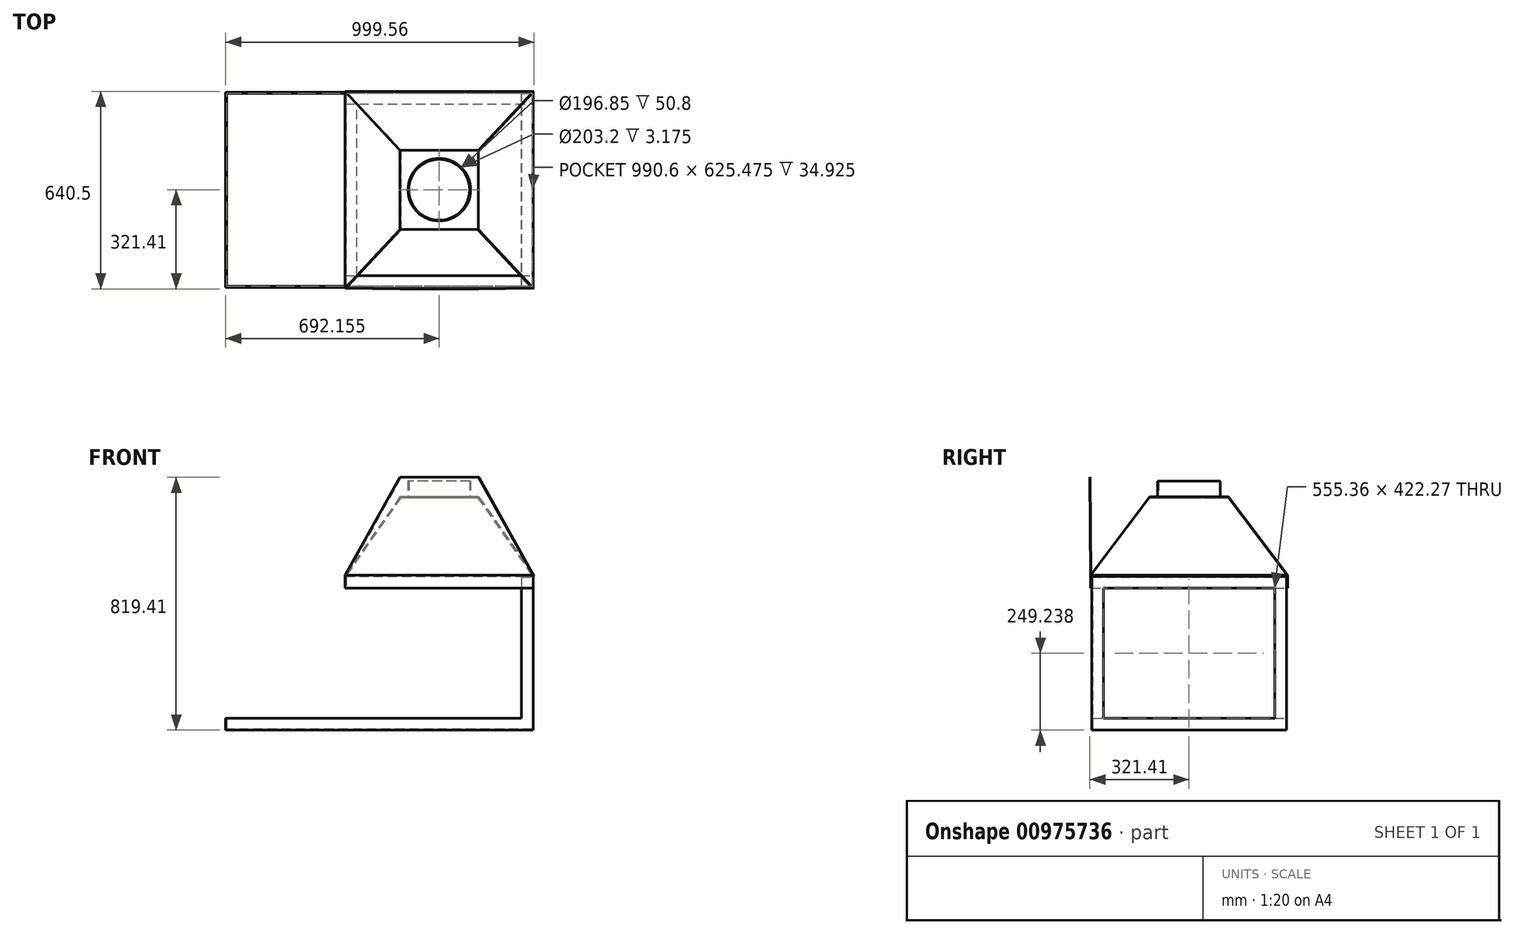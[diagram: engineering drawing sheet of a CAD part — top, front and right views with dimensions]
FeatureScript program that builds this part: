
annotation { "Feature Type Name" : "Feature", "Feature Type Description" : "" }
export const myFeature = defineFeature(function(context is Context, id is Id, definition is map)
    precondition{}
    {
        {
            var Q0;
            Q0=qCreatedBy(makeId("Top.planeOp"),FACE);
            var sketch = newSketch(context, id + "F0", { "sketchPlane" : qUnion([Q0])});
            skLineSegment(sketch, "E0.bottom", {"start": v(498.48, -315.91) * mm, "end": v(-498.48, -315.91) * mm});
            skLineSegment(sketch, "E0.top", {"start": v(498.48, 315.91) * mm, "end": v(-498.48, 315.91) * mm});
            skLineSegment(sketch, "E0.left", {"start": v(498.48, -315.91) * mm, "end": v(498.48, 315.91) * mm});
            skLineSegment(sketch, "E0.right", {"start": v(-498.48, -315.91) * mm, "end": v(-498.48, 315.91) * mm});
            skPoint(sketch, "E0.middle", {"position": v(0, 0) * mm});
            skLineSegment(sketch, "E1.0", {"start": v(495.3, 312.74) * mm, "end": v(-495.3, 312.74) * mm});
            skLineSegment(sketch, "E1.1", {"start": v(495.3, -312.74) * mm, "end": v(495.3, 312.74) * mm});
            skLineSegment(sketch, "E1.2", {"start": v(495.3, -312.74) * mm, "end": v(-495.3, -312.74) * mm});
            skLineSegment(sketch, "E1.3", {"start": v(-495.3, -312.74) * mm, "end": v(-495.3, 312.74) * mm});
            skSolve(sketch);
        }
        {
            var Q0;
            Q0=makeQuery(id+"F0.imprint","IMPRINT",FACE,{"disambiguationData":[TD([[makeQuery(id+"F0.imprint","IMPRINT",EDGE,{"derivedFrom":sQuery(id+"F0.wireOp",EDGE,"E0.bottom")}),-1.0]])]});
            extrude(context, id + "F1", {"entities" : qUnion([Q0]), "depth" : 38.1 * mm, "offsetDistance" : 25.4 * mm});
        }
        {
            var Q0;
            Q0=makeQuery(id+"F1.opExtrude","CAP_FACE",FACE,{"disambiguationData":[OSD([sQuery(id+"F0.wireOp",EDGE,"E0.bottom"),sQuery(id+"F0.wireOp",EDGE,"E0.top"),sQuery(id+"F0.wireOp",EDGE,"E0.left"),sQuery(id+"F0.wireOp",EDGE,"E0.right"),sQuery(id+"F0.wireOp",EDGE,"E1.0"),sQuery(id+"F0.wireOp",EDGE,"E1.1"),sQuery(id+"F0.wireOp",EDGE,"E1.2"),sQuery(id+"F0.wireOp",EDGE,"E1.3")])],"isStart":false});
            var sketch = newSketch(context, id + "F2", { "sketchPlane" : qUnion([Q0])});
            skLineSegment(sketch, "E2", {"start": v(496.98, 315.91) * mm, "end": v(496.98, 277.81) * mm, "construction": true});
            skLineSegment(sketch, "E3", {"start": v(498.48, 314.56) * mm, "end": v(460.38, 314.56) * mm, "construction": true});
            skLineSegment(sketch, "E4", {"start": v(460.38, 315.91) * mm, "end": v(460.38, 312.74) * mm});
            skLineSegment(sketch, "E5", {"start": v(460.38, 312.74) * mm, "end": v(495.3, 312.74) * mm});
            skLineSegment(sketch, "E6", {"start": v(495.3, 312.74) * mm, "end": v(495.3, 277.81) * mm});
            skLineSegment(sketch, "E7", {"start": v(495.3, 277.68) * mm, "end": v(498.48, 277.68) * mm});
            skLineSegment(sketch, "E8", {"start": v(498.48, 277.68) * mm, "end": v(498.48, 315.91) * mm});
            skLineSegment(sketch, "E9", {"start": v(498.48, 315.91) * mm, "end": v(460.38, 315.91) * mm});
            skSolve(sketch);
        }
        {
            var Q0;
            Q0=makeQuery(id+"F2.imprint","IMPRINT",FACE,{"disambiguationData":[TD([[makeQuery(id+"F2.imprint","IMPRINT",EDGE,{"derivedFrom":sQuery(id+"F2.wireOp",EDGE,"E4")}),1.0]])]});
            extrude(context, id + "F3", {"entities" : qUnion([Q0]), "depth" : 460.38 * mm, "offsetDistance" : 25.4 * mm});
        }
        {
            var Q0;
            Q0=makeQuery(id+"F3.opExtrude","SWEPT_BODY",BODY,{"disambiguationData":[OSD([sQuery(id+"F0.wireOp",EDGE,"E1.1"),sQuery(id+"F2.wireOp",EDGE,"E4"),sQuery(id+"F2.wireOp",EDGE,"E5"),sQuery(id+"F2.wireOp",EDGE,"E6"),sQuery(id+"F2.wireOp",EDGE,"E7"),sQuery(id+"F2.wireOp",EDGE,"E8"),sQuery(id+"F2.wireOp",EDGE,"E9")])]});
            var Q1;
            Q1=qCreatedBy(makeId("Front.planeOp"),FACE);
            mirror(context, id + "F4", {"operationType" : NewBodyOperationType.ADD, "entities" : qUnion([Q0]), "mirrorPlane" : qUnion([Q1])});
        }
        {
            var Q0;
            Q0=makeQuery(id+"F3.opExtrude","SWEPT_FACE",FACE,{"disambiguationData":[OSD([sQuery(id+"F2.wireOp",EDGE,"E7")])]});
            var sketch = newSketch(context, id + "F5", { "sketchPlane" : qUnion([Q0])});
            skLineSegment(sketch, "E10", {"start": v(496.89, 498.48) * mm, "end": v(496.89, 460.38) * mm, "construction": true});
            skLineSegment(sketch, "E11", {"start": v(495.3, 460.38) * mm, "end": v(498.48, 460.38) * mm});
            skLineSegment(sketch, "E12", {"start": v(495.3, 460.38) * mm, "end": v(495.3, 498.48) * mm});
            skLineSegment(sketch, "E13", {"start": v(495.3, 498.48) * mm, "end": v(498.48, 498.48) * mm});
            skLineSegment(sketch, "E14", {"start": v(498.48, 498.48) * mm, "end": v(498.48, 460.38) * mm});
            skSolve(sketch);
        }
        {
            var Q0;
            Q0=makeQuery(id+"F4.boolean.opBoolean","MERGE",FACE,{"derivedFrom":[makeQuery(id+"F1.opExtrude","SWEPT_FACE",FACE,{"disambiguationData":[OSD([sQuery(id+"F0.wireOp",EDGE,"E1.0")])]}),makeQuery(id+"F3.opExtrude","SWEPT_FACE",FACE,{"disambiguationData":[OSD([sQuery(id+"F2.wireOp",EDGE,"E5")])]})]});
            var sketch = newSketch(context, id + "F6", { "sketchPlane" : qUnion([Q0])});
            skPoint(sketch, "E15.0", {"position": v(477.84, 498.48) * mm});
            skLineSegment(sketch, "E16", {"start": v(477.84, 498.48) * mm, "end": v(477.84, 495.3) * mm, "construction": true});
            skLineSegment(sketch, "E17", {"start": v(460.38, 495.3) * mm, "end": v(495.3, 495.3) * mm});
            skLineSegment(sketch, "E18", {"start": v(495.3, 495.3) * mm, "end": v(495.3, 498.48) * mm});
            skLineSegment(sketch, "E19", {"start": v(495.3, 498.48) * mm, "end": v(460.38, 498.48) * mm});
            skLineSegment(sketch, "E20", {"start": v(460.38, 498.48) * mm, "end": v(460.38, 495.3) * mm});
            skSolve(sketch);
        }
        {
            var Q0;
            Q0=makeQuery(id+"F6.imprint","IMPRINT",FACE,{"disambiguationData":[TD([[makeQuery(id+"F6.imprint","IMPRINT",EDGE,{"derivedFrom":sQuery(id+"F6.wireOp",EDGE,"E17")}),1.0]])]});
            var Q1;
            Q1=makeQuery(id+"F4.boolean.opBoolean","MERGE",FACE,{"derivedFrom":[makeQuery(id+"F1.opExtrude","SWEPT_FACE",FACE,{"disambiguationData":[OSD([sQuery(id+"F0.wireOp",EDGE,"E1.2")])]}),makeQuery(id+"F4.opPattern","COPY",FACE,{"derivedFrom":makeQuery(id+"F3.opExtrude","SWEPT_FACE",FACE,{"disambiguationData":[OSD([sQuery(id+"F2.wireOp",EDGE,"E5")])]}),"instanceName":"1"})]});
            extrude(context, id + "F7", {"entities" : qUnion([Q0]), "operationType" : NewBodyOperationType.ADD, "endBound" : BoundingType.UP_TO_SURFACE, "depth" : 25.4 * mm, "endBoundEntityFace" : qUnion([Q1]), "offsetDistance" : 25.4 * mm});
        }
        {
            var Q0;
            Q0=makeQuery(id+"F5.imprint","IMPRINT",FACE,{"disambiguationData":[TD([[makeQuery(id+"F5.imprint","IMPRINT",EDGE,{"derivedFrom":sQuery(id+"F5.wireOp",EDGE,"E11")}),1.0]])]});
            var Q1;
            Q1=makeQuery(id+"F4.opPattern","COPY",FACE,{"derivedFrom":makeQuery(id+"F3.opExtrude","SWEPT_FACE",FACE,{"disambiguationData":[OSD([sQuery(id+"F2.wireOp",EDGE,"E7")])]}),"instanceName":"1"});
            extrude(context, id + "F8", {"entities" : qUnion([Q0]), "operationType" : NewBodyOperationType.ADD, "endBound" : BoundingType.UP_TO_SURFACE, "depth" : 25.4 * mm, "endBoundEntityFace" : qUnion([Q1]), "offsetDistance" : 25.4 * mm});
        }
        {
            var Q0;
            {var subQ0=makeQuery(id+"F3.opExtrude","SWEPT_FACE",FACE,{"disambiguationData":[OSD([sQuery(id+"F2.wireOp",EDGE,"E8")])]});Q0=makeQuery(id+"F8.boolean.opBoolean","MERGE",FACE,{"derivedFrom":[makeQuery(id+"F4.boolean.opBoolean","MERGE",FACE,{"derivedFrom":[makeQuery(id+"F1.opExtrude","SWEPT_FACE",FACE,{"disambiguationData":[OSD([sQuery(id+"F0.wireOp",EDGE,"E0.left")])]}),subQ0,makeQuery(id+"F4.opPattern","COPY",FACE,{"derivedFrom":subQ0,"instanceName":"1"})]}),makeQuery(id+"F8.opExtrude","SWEPT_FACE",FACE,{"disambiguationData":[OSD([sQuery(id+"F5.wireOp",EDGE,"E14")])]})]});}
            var sketch = newSketch(context, id + "F9", { "sketchPlane" : qUnion([Q0])});
            skPoint(sketch, "E21.0", {"position": v(315.91, 498.48) * mm});
            skLineSegment(sketch, "E22", {"start": v(315.91, 498.48) * mm, "end": v(277.81, 498.48) * mm});
            skLineSegment(sketch, "E23", {"start": v(315.91, 498.48) * mm, "end": v(315.91, 460.38) * mm});
            skLineSegment(sketch, "E24", {"start": v(315.91, 460.38) * mm, "end": v(319.09, 460.38) * mm});
            skLineSegment(sketch, "E25", {"start": v(277.81, 498.48) * mm, "end": v(277.81, 501.65) * mm});
            skLineSegment(sketch, "E26", {"start": v(277.81, 501.65) * mm, "end": v(319.09, 501.65) * mm});
            skLineSegment(sketch, "E27", {"start": v(319.09, 501.65) * mm, "end": v(319.09, 460.38) * mm});
            skSolve(sketch);
        }
        {
            var Q0;
            Q0=makeQuery(id+"F9.imprint","IMPRINT",FACE,{"disambiguationData":[TD([[makeQuery(id+"F9.imprint","IMPRINT",EDGE,{"derivedFrom":sQuery(id+"F9.wireOp",EDGE,"E22")}),1.0]])]});
            extrude(context, id + "F10", {"entities" : qUnion([Q0]), "oppositeDirection" : true, "depth" : 609.6 * mm, "offsetDistance" : 25.4 * mm});
        }
        {
            var Q0;
            Q0=makeQuery(id+"F10.opExtrude","SWEPT_BODY",BODY,{"disambiguationData":[OSD([sQuery(id+"F9.wireOp",EDGE,"E22"),sQuery(id+"F9.wireOp",EDGE,"E23"),sQuery(id+"F9.wireOp",EDGE,"E24"),sQuery(id+"F9.wireOp",EDGE,"E25"),sQuery(id+"F9.wireOp",EDGE,"E26"),sQuery(id+"F9.wireOp",EDGE,"E27")])]});
            var Q1;
            Q1=qCreatedBy(makeId("Front.planeOp"),FACE);
            mirror(context, id + "F11", {"entities" : qUnion([Q0]), "mirrorPlane" : qUnion([Q1])});
        }
        {
            var Q0;
            Q0=makeQuery(id+"F10.opExtrude","SWEPT_FACE",FACE,{"disambiguationData":[OSD([sQuery(id+"F9.wireOp",EDGE,"E23")])]});
            var sketch = newSketch(context, id + "F12", { "sketchPlane" : qUnion([Q0])});
            skPoint(sketch, "E28.0", {"position": v(-111.13, 460.38) * mm});
            skLineSegment(sketch, "E29", {"start": v(-111.13, 460.37) * mm, "end": v(-107.95, 460.37) * mm});
            skLineSegment(sketch, "E30", {"start": v(-107.95, 460.37) * mm, "end": v(-107.95, 498.48) * mm});
            skLineSegment(sketch, "E31", {"start": v(-107.95, 498.48) * mm, "end": v(-111.12, 498.48) * mm});
            skLineSegment(sketch, "E32", {"start": v(-111.12, 498.48) * mm, "end": v(-111.13, 460.38) * mm});
            skSolve(sketch);
        }
        {
            var Q0;
            Q0=makeQuery(id+"F12.imprint","IMPRINT",FACE,{"disambiguationData":[TD([[makeQuery(id+"F12.imprint","IMPRINT",EDGE,{"derivedFrom":sQuery(id+"F12.wireOp",EDGE,"E29")}),1.0]])]});
            var Q1;
            Q1=makeQuery(id+"F11.opPattern","COPY",FACE,{"derivedFrom":makeQuery(id+"F10.opExtrude","SWEPT_FACE",FACE,{"disambiguationData":[OSD([sQuery(id+"F9.wireOp",EDGE,"E23")])]}),"instanceName":"1"});
            extrude(context, id + "F13", {"entities" : qUnion([Q0]), "endBound" : BoundingType.UP_TO_SURFACE, "depth" : 25.4 * mm, "endBoundEntityFace" : qUnion([Q1]), "offsetDistance" : 25.4 * mm});
        }
        {
            var Q0;
            Q0=makeQuery(id+"F10.opExtrude","SWEPT_FACE",FACE,{"disambiguationData":[OSD([sQuery(id+"F9.wireOp",EDGE,"E25")])]});
            var sketch = newSketch(context, id + "F14", { "sketchPlane" : qUnion([Q0])});
            skLineSegment(sketch, "E33", {"start": v(-111.13, 500.06) * mm, "end": v(-73.03, 500.06) * mm, "construction": true});
            skLineSegment(sketch, "E34", {"start": v(-73.03, 501.65) * mm, "end": v(-73.03, 498.48) * mm});
            skLineSegment(sketch, "E35", {"start": v(-73.03, 498.48) * mm, "end": v(-111.12, 498.48) * mm});
            skLineSegment(sketch, "E36", {"start": v(-111.13, 498.48) * mm, "end": v(-111.13, 501.65) * mm});
            skLineSegment(sketch, "E37", {"start": v(-111.13, 501.65) * mm, "end": v(-73.03, 501.65) * mm});
            skSolve(sketch);
        }
        {
            var Q0;
            Q0=makeQuery(id+"F14.imprint","IMPRINT",FACE,{"disambiguationData":[TD([[makeQuery(id+"F14.imprint","IMPRINT",EDGE,{"derivedFrom":sQuery(id+"F14.wireOp",EDGE,"E34")}),-1.0]])]});
            var Q1;
            Q1=makeQuery(id+"F11.opPattern","COPY",FACE,{"derivedFrom":makeQuery(id+"F10.opExtrude","SWEPT_FACE",FACE,{"disambiguationData":[OSD([sQuery(id+"F9.wireOp",EDGE,"E25")])]}),"instanceName":"1"});
            extrude(context, id + "F15", {"entities" : qUnion([Q0]), "endBound" : BoundingType.UP_TO_SURFACE, "depth" : 25.4 * mm, "endBoundEntityFace" : qUnion([Q1]), "offsetDistance" : 25.4 * mm});
        }
        {
            var Q0;
            Q0=makeQuery(id+"F11.opPattern","COPY",FACE,{"derivedFrom":makeQuery(id+"F10.opExtrude","SWEPT_FACE",FACE,{"disambiguationData":[OSD([sQuery(id+"F9.wireOp",EDGE,"E26")])]}),"instanceName":"1"});
            var sketch = newSketch(context, id + "F16", { "sketchPlane" : qUnion([Q0])});
            skPoint(sketch, "E38.0", {"position": v(498.48, -319.09) * mm});
            skPoint(sketch, "E39.0", {"position": v(-111.13, 319.09) * mm});
            skPoint(sketch, "E40.0", {"position": v(498.48, 319.09) * mm});
            skPoint(sketch, "E41.0", {"position": v(-111.13, -319.09) * mm});
            skPoint(sketch, "E42.0", {"position": v(193.67, 319.09) * mm});
            skLineSegment(sketch, "E43", {"start": v(193.67, 319.09) * mm, "end": v(193.67, -319.09) * mm, "construction": true});
            skCircle(sketch, "E44", {"center": v(193.67, 0) * mm, "radius": 76.2 * mm});
            skSolve(sketch);
        }
        {
            var Q0;
            Q0=qCreatedBy(makeId("Front.planeOp"),FACE);
            var sketch = newSketch(context, id + "F17", { "sketchPlane" : qUnion([Q0])});
            skPoint(sketch, "E45.0", {"position": v(193.67, 501.65) * mm});
            skLineSegment(sketch, "E46", {"start": v(193.67, 501.65) * mm, "end": v(193.67, 755.65) * mm, "construction": true});
            skSolve(sketch);
        }
        {
            var Q0;
            Q0=makeQuery(id+"F10.opExtrude","SWEPT_FACE",FACE,{"disambiguationData":[OSD([sQuery(id+"F9.wireOp",EDGE,"E26")])]});
            cPlane(context, id + "F18", {"entities" : qUnion([Q0]), "cplaneType" : CPlaneType.OFFSET, "offset" : 254 * mm, "width" : 152.4 * mm, "height" : 152.4 * mm});
        }
        {
            var Q0;
            Q0=qCreatedBy(id+"F18.planeOp",FACE);
            var sketch = newSketch(context, id + "F19", { "sketchPlane" : qUnion([Q0])});
            skPoint(sketch, "E47.0", {"position": v(193.67, 0) * mm});
            skCircle(sketch, "E48", {"center": v(193.67, 0) * mm, "radius": 101.6 * mm});
            skLineSegment(sketch, "E49.bottom", {"start": v(320.67, -128.15) * mm, "end": v(66.67, -128.15) * mm});
            skLineSegment(sketch, "E49.top", {"start": v(320.67, 128.15) * mm, "end": v(66.67, 128.15) * mm});
            skLineSegment(sketch, "E49.left", {"start": v(320.67, -128.15) * mm, "end": v(320.67, 128.15) * mm});
            skLineSegment(sketch, "E49.right", {"start": v(66.67, -128.15) * mm, "end": v(66.67, 128.15) * mm});
            skSolve(sketch);
        }
        {
            var Q0;
            Q0=sQuery(id+"F19.wireOp",VERTEX,"E49.bottom.end");
            var Q1;
            Q1=sQuery(id+"F16.wireOp",VERTEX,"E41.0");
            var Q2;
            Q2=sQuery(id+"F16.wireOp",VERTEX,"E38.0");
            cPlane(context, id + "F20", {"entities" : qUnion([Q0, Q1, Q2]), "cplaneType" : CPlaneType.THREE_POINT, "offset" : 25.4 * mm, "width" : 152.4 * mm, "height" : 152.4 * mm});
        }
        {
            var Q0;
            Q0=qCreatedBy(id+"F20.planeOp",FACE);
            var sketch = newSketch(context, id + "F21", { "sketchPlane" : qUnion([Q0])});
            skPoint(sketch, "E50.0", {"position": v(-66.67, 527.02) * mm});
            skPoint(sketch, "E51.0", {"position": v(111.13, 209.25) * mm});
            skPoint(sketch, "E52.0", {"position": v(-320.67, 527.02) * mm});
            skPoint(sketch, "E53.0", {"position": v(-498.48, 209.25) * mm});
            skLineSegment(sketch, "E54", {"start": v(-66.67, 527.02) * mm, "end": v(111.13, 209.25) * mm});
            skLineSegment(sketch, "E55", {"start": v(-320.67, 527.02) * mm, "end": v(-498.47, 209.25) * mm});
            skLineSegment(sketch, "E56", {"start": v(-498.47, 209.25) * mm, "end": v(111.13, 209.25) * mm});
            skLineSegment(sketch, "E57", {"start": v(-66.67, 527.02) * mm, "end": v(-320.67, 527.02) * mm});
            skSolve(sketch);
        }
        {
            var Q0;
            Q0=sQuery(id+"F19.wireOp",VERTEX,"E49.top.end");
            var Q1;
            Q1=sQuery(id+"F16.wireOp",VERTEX,"E39.0");
            var Q2;
            Q2=sQuery(id+"F16.wireOp",VERTEX,"E41.0");
            cPlane(context, id + "F22", {"entities" : qUnion([Q0, Q1, Q2]), "cplaneType" : CPlaneType.THREE_POINT, "offset" : 25.4 * mm, "width" : 152.4 * mm, "height" : 152.4 * mm});
        }
        {
            var Q0;
            Q0=qCreatedBy(id+"F22.planeOp",FACE);
            var sketch = newSketch(context, id + "F23", { "sketchPlane" : qUnion([Q0])});
            skPoint(sketch, "E58.0", {"position": v(128.15, 657.29) * mm});
            skPoint(sketch, "E59.0", {"position": v(-128.15, 657.29) * mm});
            skPoint(sketch, "E60.0", {"position": v(319.09, 347.24) * mm});
            skPoint(sketch, "E61.0", {"position": v(-319.09, 347.24) * mm});
            skLineSegment(sketch, "E62", {"start": v(128.15, 657.29) * mm, "end": v(319.09, 347.24) * mm});
            skLineSegment(sketch, "E63", {"start": v(128.15, 657.29) * mm, "end": v(-128.15, 657.29) * mm});
            skLineSegment(sketch, "E64", {"start": v(-128.15, 657.29) * mm, "end": v(-319.09, 347.24) * mm});
            skLineSegment(sketch, "E65", {"start": v(-319.09, 347.24) * mm, "end": v(319.09, 347.24) * mm});
            skSolve(sketch);
        }
        {
            var Q0;
            Q0=makeQuery(id+"F23.imprint","IMPRINT",FACE,{"disambiguationData":[TD([[makeQuery(id+"F23.imprint","IMPRINT",EDGE,{"derivedFrom":sQuery(id+"F23.wireOp",EDGE,"E62")}),-1.0]])]});
            var Q1;
            Q1=makeQuery(id+"F21.imprint","IMPRINT",FACE,{"disambiguationData":[TD([[makeQuery(id+"F21.imprint","IMPRINT",EDGE,{"derivedFrom":sQuery(id+"F21.wireOp",EDGE,"E54")}),-1.0]])]});
            extrude(context, id + "F24", {"entities" : qUnion([Q0, Q1]), "depth" : 3.17 * mm, "offsetDistance" : 25.4 * mm});
        }
        {
            var Q0;
            Q0=makeQuery(id+"F24.opExtrude","SWEPT_BODY",BODY,{"disambiguationData":[OSD([sQuery(id+"F21.wireOp",EDGE,"E54"),sQuery(id+"F21.wireOp",EDGE,"E55"),sQuery(id+"F21.wireOp",EDGE,"E56"),sQuery(id+"F21.wireOp",EDGE,"E57")])]});
            var Q1;
            Q1=qCreatedBy(makeId("Front.planeOp"),FACE);
            mirror(context, id + "F25", {"entities" : qUnion([Q0]), "mirrorPlane" : qUnion([Q1])});
        }
        {
            var Q0;
            Q0=sQuery(id+"F17.wireOp",EDGE,"E46");
            cPlane(context, id + "F26", {"entities" : qUnion([Q0]), "cplaneType" : CPlaneType.LINE_ANGLE, "offset" : 25.4 * mm, "angle" : 0 * degree, "width" : 152.4 * mm, "height" : 152.4 * mm});
        }
        {
            var Q0;
            Q0=makeQuery(id+"F24.opExtrude","SWEPT_BODY",BODY,{"disambiguationData":[OSD([sQuery(id+"F23.wireOp",EDGE,"E62"),sQuery(id+"F23.wireOp",EDGE,"E63"),sQuery(id+"F23.wireOp",EDGE,"E64"),sQuery(id+"F23.wireOp",EDGE,"E65")])]});
            var Q1;
            Q1=qCreatedBy(id+"F26.planeOp",FACE);
            mirror(context, id + "F27", {"entities" : qUnion([Q0]), "mirrorPlane" : qUnion([Q1])});
        }
        {
            var Q0;
            Q0=makeQuery(id+"F19.imprint","IMPRINT",FACE,{"disambiguationData":[TD([[makeQuery(id+"F19.imprint","IMPRINT",EDGE,{"derivedFrom":sQuery(id+"F19.wireOp",EDGE,"E48")}),-1.0]])]});
            extrude(context, id + "F28", {"entities" : qUnion([Q0]), "oppositeDirection" : true, "depth" : 3.17 * mm, "offsetDistance" : 25.4 * mm});
        }
        {
            var Q0;
            Q0=makeQuery(id+"F28.opExtrude","CAP_FACE",FACE,{"disambiguationData":[OSD([sQuery(id+"F19.wireOp",EDGE,"E48"),sQuery(id+"F19.wireOp",EDGE,"E49.bottom"),sQuery(id+"F19.wireOp",EDGE,"E49.top"),sQuery(id+"F19.wireOp",EDGE,"E49.left"),sQuery(id+"F19.wireOp",EDGE,"E49.right")])],"isStart":true});
            var sketch = newSketch(context, id + "F29", { "sketchPlane" : qUnion([Q0])});
            skCircle(sketch, "E66.0", {"center": v(193.67, 0) * mm, "radius": 101.6 * mm});
            skCircle(sketch, "E67.0", {"center": v(193.67, 0) * mm, "radius": 98.43 * mm});
            skSolve(sketch);
        }
        {
            var Q0;
            Q0=makeQuery(id+"F29.imprint","IMPRINT",FACE,{"disambiguationData":[TD([[makeQuery(id+"F29.imprint","IMPRINT",EDGE,{"derivedFrom":sQuery(id+"F29.wireOp",EDGE,"E66.0")}),1.0]])]});
            extrude(context, id + "F30", {"entities" : qUnion([Q0]), "depth" : 50.8 * mm, "offsetDistance" : 25.4 * mm});
        }
        {
            var Q0;
            Q0=makeQuery(id+"F0.imprint","IMPRINT",FACE,{"disambiguationData":[TD([[makeQuery(id+"F0.imprint","IMPRINT",EDGE,{"derivedFrom":sQuery(id+"F0.wireOp",EDGE,"E1.0")}),1.0]])]});
            extrude(context, id + "F31", {"entities" : qUnion([Q0]), "operationType" : NewBodyOperationType.ADD, "depth" : 3.17 * mm, "offsetDistance" : 25.4 * mm});
        }
        {
            var Q0;
            Q0=makeQuery(id+"F24.opExtrude","SWEPT_BODY",BODY,{"disambiguationData":[OSD([sQuery(id+"F21.wireOp",EDGE,"E54"),sQuery(id+"F21.wireOp",EDGE,"E55"),sQuery(id+"F21.wireOp",EDGE,"E56"),sQuery(id+"F21.wireOp",EDGE,"E57")])]});
            var Q1;
            Q1=makeQuery(id+"F11.opPattern","COPY",EDGE,{"derivedFrom":makeQuery(id+"F10.opExtrude","SWEPT_EDGE",EDGE,{"disambiguationData":[OSD([sQuery(id+"F9.wireOp",EDGE,"E26"),sQuery(id+"F9.wireOp",EDGE,"E27")])]}),"instanceName":"1"});
            transform(context, id + "F32", {"entities" : qUnion([Q0]), "transformType" : TransformType.ROTATION, "transformAxis" : qUnion([Q1]), "angle" : 37.35 * degree, "makeCopy" : false});
        }
    });
